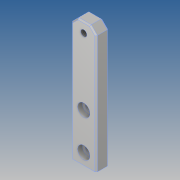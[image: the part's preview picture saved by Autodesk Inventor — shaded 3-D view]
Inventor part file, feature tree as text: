
AUTODESK INVENTOR PART (.ipt)
format: ipt  version: 2018.2 (Build 222227000, 227)  size: 121,856 bytes
history: native  units: mm
features: sketch x3, chamfer x2, extrude x1, hole x1
ambient origin geometry x8: Origin, YZ Plane, XZ Plane, XY Plane, X Axis, Y Axis, Z Axis, Center Point
bodies: Body1 (feature_tree)
feature tree (7):
  extrude  "Grundkörper"  Depth=20.0mm
  hole  "DIN7984_M5"  [1 undecoded]
  chamfer  "Fase_Abschraegung"  Distance=8.0mm
  chamfer  "Fase_Allgemein"  Distance=5.0mm Angle=45.0deg
  sketch  "Skizze8"  dims[d49=10.0mm d50=20.0mm]
  sketch  "Skizze9"  dims[d51=100.0mm d52=0.0mm d53=9.0mm]
  sketch  "Skizze10"  dims[d54=38.5mm d55=5.5mm d56=6.0mm d57=10.0mm d58=3.9mm d59=90.0deg d60=8.0mm d61=20.594885mm d62=8.0mm d63=4.917mm d64=12.0mm d65=6.0mm d66=2.0mm d67=90.0deg d68=17.1mm d69=20.594885mm d73=5.0mm d74=2.0mm d75=45.0deg d76=1.0mm d77=2.0mm d78=45.0deg]
note: 1 required parameter value undecoded (feature->parameter linkage not recoverable at this tier; creation-order binding heuristic only, values carry confidence <= 0.55)
